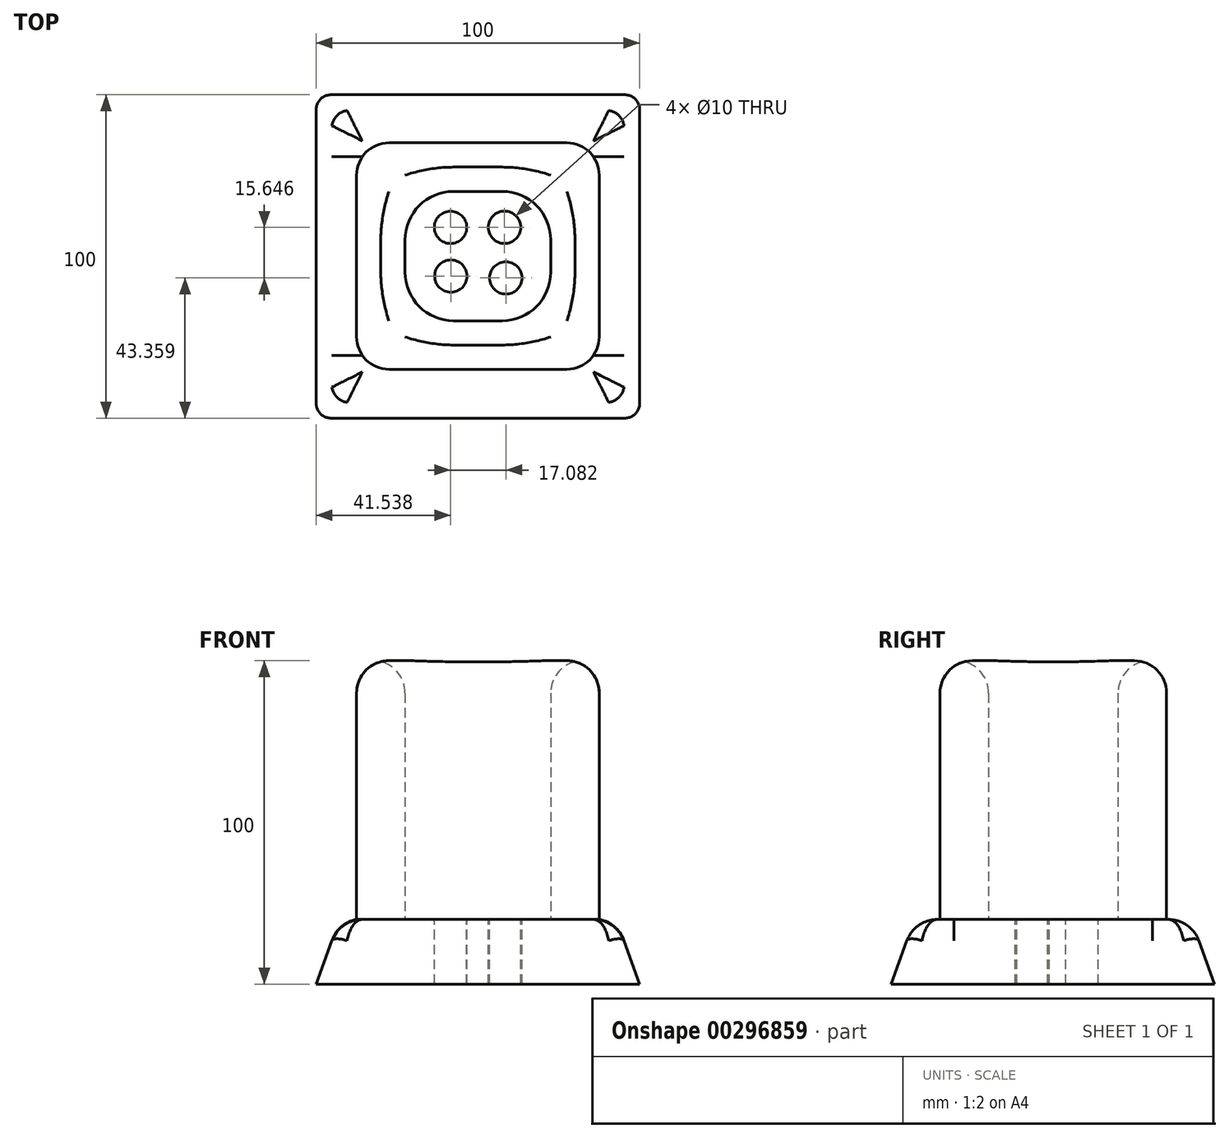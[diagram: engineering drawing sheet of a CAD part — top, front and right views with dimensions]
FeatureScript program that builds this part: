
annotation { "Feature Type Name" : "Feature", "Feature Type Description" : "" }
export const myFeature = defineFeature(function(context is Context, id is Id, definition is map)
    precondition{}
    {
        {
            var Q0;
            Q0=qCreatedBy(makeId("Top.planeOp"),FACE);
            var sketch = newSketch(context, id + "F0", { "sketchPlane" : qUnion([Q0])});
            skLineSegment(sketch, "E0.bottom", {"start": v(-50.14, 48.64) * mm, "end": v(49.86, 48.64) * mm});
            skLineSegment(sketch, "E0.top", {"start": v(-50.14, -51.36) * mm, "end": v(49.86, -51.36) * mm});
            skLineSegment(sketch, "E0.left", {"start": v(-50.14, 48.64) * mm, "end": v(-50.14, -51.36) * mm});
            skLineSegment(sketch, "E0.right", {"start": v(49.86, 48.64) * mm, "end": v(49.86, -51.36) * mm});
            skSolve(sketch);
        }
        {
            var Q0;
            Q0=makeQuery(id+"F0.imprint","IMPRINT",FACE,{"disambiguationData":[TD([[makeQuery(id+"F0.imprint","IMPRINT",EDGE,{"derivedFrom":sQuery(id+"F0.wireOp",EDGE,"E0.bottom")}),-1.0]])]});
            var Q1;
            Q1=sQuery(id+"F0.wireOp",EDGE,"E0.top");
            var Q2;
            Q2=sQuery(id+"F0.wireOp",EDGE,"E0.left");
            var Q3;
            Q3=sQuery(id+"F0.wireOp",EDGE,"E0.right");
            var Q4;
            Q4=sQuery(id+"F0.wireOp",EDGE,"E0.bottom");
            extrude(context, id + "F1", {"entities" : qUnion([Q0]), "surfaceEntities" : qUnion([Q1, Q2, Q3, Q4]), "depth" : 20 * mm, "hasDraft" : true, "draftAngle" : 20 * degree, "draftPullDirection" : true});
        }
        {
            var Q0;
            Q0=makeQuery(id+"F1.opExtrude","CAP_FACE",FACE,{"disambiguationData":[OSD([sQuery(id+"F0.wireOp",EDGE,"E0.bottom"),sQuery(id+"F0.wireOp",EDGE,"E0.top"),sQuery(id+"F0.wireOp",EDGE,"E0.left"),sQuery(id+"F0.wireOp",EDGE,"E0.right")])],"isStart":false});
            var sketch = newSketch(context, id + "F2", { "sketchPlane" : qUnion([Q0])});
            skLineSegment(sketch, "E1.bottom", {"start": v(-27.65, 33.76) * mm, "end": v(27.35, 33.76) * mm});
            skLineSegment(sketch, "E1.top", {"start": v(-27.65, -36.24) * mm, "end": v(27.35, -36.24) * mm});
            skLineSegment(sketch, "E1.left", {"start": v(-37.65, 23.76) * mm, "end": v(-37.65, -26.24) * mm});
            skLineSegment(sketch, "E1.right", {"start": v(37.35, 23.76) * mm, "end": v(37.35, -26.24) * mm});
            skLineSegment(sketch, "E2.bottom", {"start": v(-7.65, 18.76) * mm, "end": v(7.35, 18.76) * mm});
            skLineSegment(sketch, "E2.top", {"start": v(-7.65, -21.24) * mm, "end": v(7.35, -21.24) * mm});
            skLineSegment(sketch, "E2.left", {"start": v(-22.65, 3.76) * mm, "end": v(-22.65, -6.24) * mm});
            skLineSegment(sketch, "E2.right", {"start": v(22.35, 3.76) * mm, "end": v(22.35, -6.24) * mm});
            skPoint(sketch, "E3.visualSharp", {"position": v(-22.65, 18.76) * mm});
            skArc(sketch, "E3.filletArc", {"start": v(-7.65, 18.76) * mm, "mid": v(-18.26, 14.37) * mm, "end": v(-22.65, 3.76) * mm});
            skPoint(sketch, "E4.visualSharp", {"position": v(22.35, 18.76) * mm});
            skArc(sketch, "E4.filletArc", {"start": v(22.35, 3.76) * mm, "mid": v(17.95, 14.37) * mm, "end": v(7.35, 18.76) * mm});
            skPoint(sketch, "E5.visualSharp", {"position": v(-22.65, -21.24) * mm});
            skArc(sketch, "E5.filletArc", {"start": v(-22.65, -6.24) * mm, "mid": v(-18.26, -16.85) * mm, "end": v(-7.65, -21.24) * mm});
            skPoint(sketch, "E6.visualSharp", {"position": v(22.35, -21.24) * mm});
            skArc(sketch, "E6.filletArc", {"start": v(7.35, -21.24) * mm, "mid": v(17.95, -16.85) * mm, "end": v(22.35, -6.24) * mm});
            skPoint(sketch, "E7.visualSharp", {"position": v(-37.65, 33.76) * mm});
            skArc(sketch, "E7.filletArc", {"start": v(-27.65, 33.76) * mm, "mid": v(-34.72, 30.83) * mm, "end": v(-37.65, 23.76) * mm});
            skPoint(sketch, "E8.visualSharp", {"position": v(37.35, 33.76) * mm});
            skArc(sketch, "E8.filletArc", {"start": v(37.35, 23.76) * mm, "mid": v(34.42, 30.83) * mm, "end": v(27.35, 33.76) * mm});
            skPoint(sketch, "E9.visualSharp", {"position": v(37.35, -36.24) * mm});
            skArc(sketch, "E9.filletArc", {"start": v(27.35, -36.24) * mm, "mid": v(34.42, -33.31) * mm, "end": v(37.35, -26.24) * mm});
            skPoint(sketch, "E10.visualSharp", {"position": v(-37.65, -36.24) * mm});
            skArc(sketch, "E10.filletArc", {"start": v(-37.65, -26.24) * mm, "mid": v(-34.72, -33.31) * mm, "end": v(-27.65, -36.24) * mm});
            skSolve(sketch);
        }
        {
            var Q0;
            Q0 = qSketchRegion(id + "F2", true);
            extrude(context, id + "F3", {"entities" : qUnion([Q0]), "operationType" : NewBodyOperationType.ADD, "depth" : 80 * mm});
        }
        {
            var Q0;
            Q0=makeQuery(id+"F1.opExtrude","CAP_EDGE",EDGE,{"disambiguationData":[OSD([sQuery(id+"F0.wireOp",EDGE,"E0.top")])],"isStart":false});
            var Q1;
            Q1=makeQuery(id+"F1.opExtrude","CAP_EDGE",EDGE,{"disambiguationData":[OSD([sQuery(id+"F0.wireOp",EDGE,"E0.right")])],"isStart":false});
            var Q2;
            Q2=makeQuery(id+"F1.opExtrude","CAP_EDGE",EDGE,{"disambiguationData":[OSD([sQuery(id+"F0.wireOp",EDGE,"E0.bottom")])],"isStart":false});
            var Q3;
            Q3=makeQuery(id+"F1.opExtrude","CAP_EDGE",EDGE,{"disambiguationData":[OSD([sQuery(id+"F0.wireOp",EDGE,"E0.left")])],"isStart":false});
            fillet(context, id + "F4", {"entities" : qUnion([Q0, Q1, Q2, Q3]), "radius" : 10 * mm, "tangentPropagation" : true, "allowEdgeOverflow" : false});
        }
        {
            var Q0;
            Q0=makeQuery(id+"F3.opExtrude","CAP_EDGE",EDGE,{"disambiguationData":[OSD([sQuery(id+"F2.wireOp",EDGE,"E1.right")])],"isStart":false});
            var Q1;
            Q1=makeQuery(id+"F3.opExtrude","CAP_EDGE",EDGE,{"disambiguationData":[OSD([sQuery(id+"F2.wireOp",EDGE,"E5.filletArc")])],"isStart":false});
            fillet(context, id + "F5", {"entities" : qUnion([Q0, Q1]), "radius" : 10 * mm, "tangentPropagation" : true, "allowEdgeOverflow" : false});
        }
        {
            var Q0;
            Q0=makeQuery(id+"F3.boolean.opBoolean","SPLIT",FACE,{"disambiguationData":[TD([makeQuery(id+"F3.opExtrude","SWEPT_FACE",FACE,{"disambiguationData":[OSD([sQuery(id+"F2.wireOp",EDGE,"E2.bottom")])]})])],"derivedFrom":makeQuery(id+"F1.opExtrude","CAP_FACE",FACE,{"disambiguationData":[OSD([sQuery(id+"F0.wireOp",EDGE,"E0.bottom"),sQuery(id+"F0.wireOp",EDGE,"E0.top"),sQuery(id+"F0.wireOp",EDGE,"E0.left"),sQuery(id+"F0.wireOp",EDGE,"E0.right")])],"isStart":false})});
            var sketch = newSketch(context, id + "F6", { "sketchPlane" : qUnion([Q0])});
            skCircle(sketch, "E11", {"center": v(-8.6, 7.63) * mm, "radius": 5 * mm});
            skCircle(sketch, "E12", {"center": v(8.08, 7.64) * mm, "radius": 5 * mm});
            skCircle(sketch, "E13", {"center": v(-8.52, -7.44) * mm, "radius": 5 * mm});
            skCircle(sketch, "E14", {"center": v(8.48, -8) * mm, "radius": 5 * mm});
            skSolve(sketch);
        }
        {
            var Q0;
            Q0 = qSketchRegion(id + "F6", true);
            extrude(context, id + "F7", {"entities" : qUnion([Q0]), "operationType" : NewBodyOperationType.REMOVE, "oppositeDirection" : true, "depth" : 25 * mm});
        }
        {
            var Q0;
            Q0=makeQuery(id+"F1.opExtrude","SWEPT_EDGE",EDGE,{"disambiguationData":[OSD([sQuery(id+"F0.wireOp",EDGE,"E0.top"),sQuery(id+"F0.wireOp",EDGE,"E0.left")])]});
            var Q1;
            Q1=makeQuery(id+"F1.opExtrude","SWEPT_EDGE",EDGE,{"disambiguationData":[OSD([sQuery(id+"F0.wireOp",EDGE,"E0.top"),sQuery(id+"F0.wireOp",EDGE,"E0.right")])]});
            var Q2;
            Q2=makeQuery(id+"F1.opExtrude","SWEPT_EDGE",EDGE,{"disambiguationData":[OSD([sQuery(id+"F0.wireOp",EDGE,"E0.bottom"),sQuery(id+"F0.wireOp",EDGE,"E0.right")])]});
            var Q3;
            Q3=makeQuery(id+"F1.opExtrude","SWEPT_EDGE",EDGE,{"disambiguationData":[OSD([sQuery(id+"F0.wireOp",EDGE,"E0.bottom"),sQuery(id+"F0.wireOp",EDGE,"E0.left")])]});
            fillet(context, id + "F8", {"entities" : qUnion([Q0, Q1, Q2, Q3]), "radius" : 5 * mm, "tangentPropagation" : true, "allowEdgeOverflow" : false});
        }
    });
